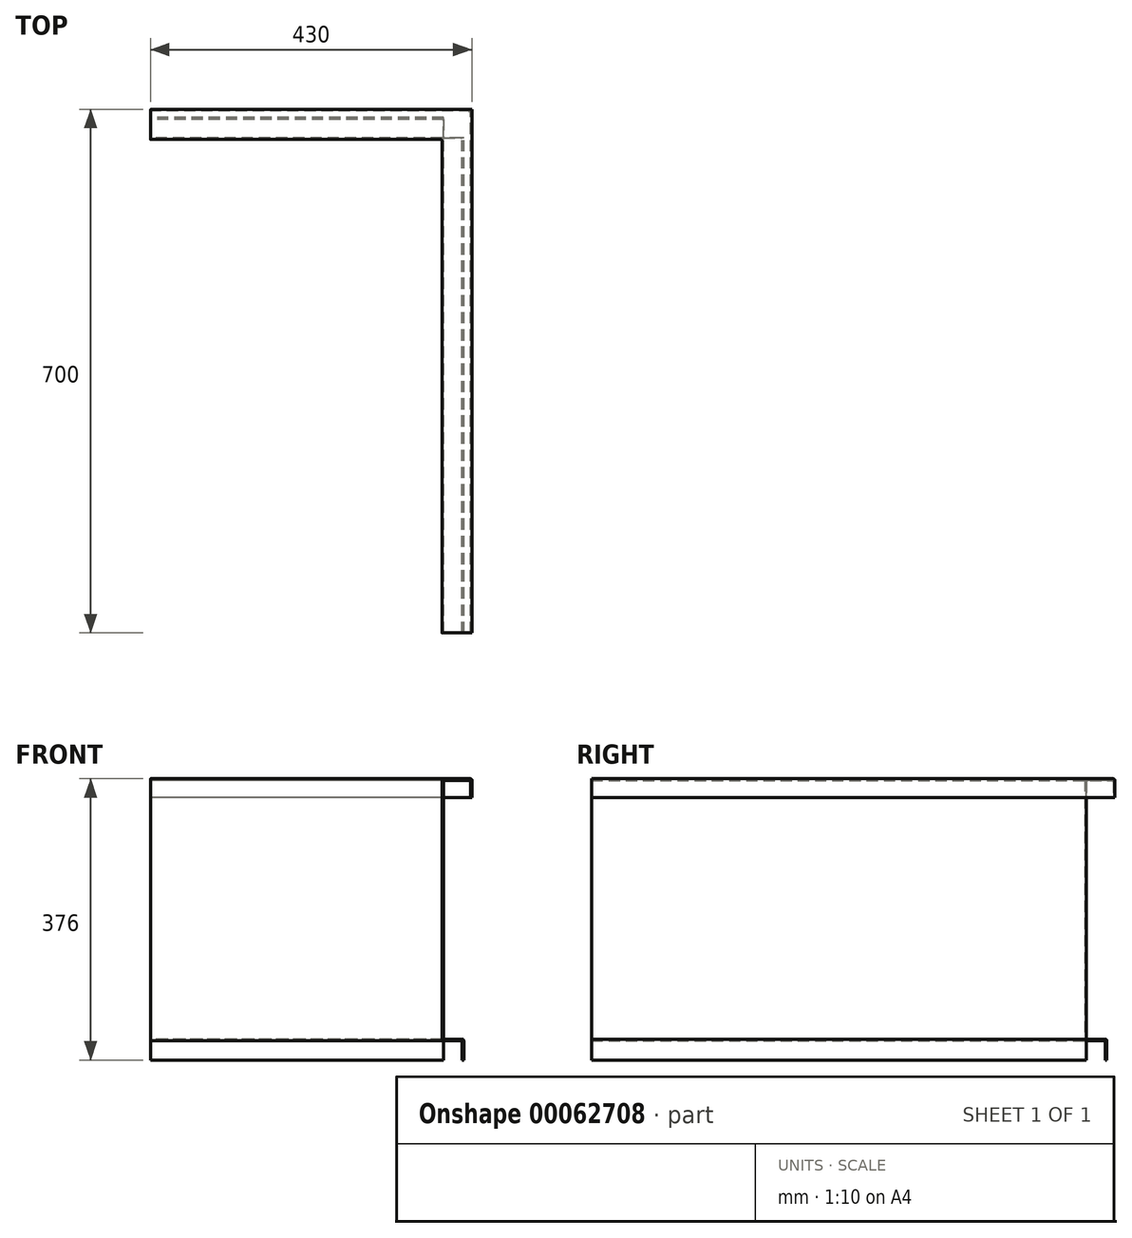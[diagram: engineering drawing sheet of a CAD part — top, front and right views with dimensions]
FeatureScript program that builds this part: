
annotation { "Feature Type Name" : "Feature", "Feature Type Description" : "" }
export const myFeature = defineFeature(function(context is Context, id is Id, definition is map)
    precondition{}
    {
        {
            var Q0;
            Q0=qCreatedBy(makeId("Front.planeOp"),FACE);
            var sketch = newSketch(context, id + "F0", { "sketchPlane" : qUnion([Q0])});
            skLineSegment(sketch, "E0", {"start": v(38, -25) * mm, "end": v(38, -2) * mm});
            skLineSegment(sketch, "E1", {"start": v(38, -2) * mm, "end": v(2, -2) * mm});
            skLineSegment(sketch, "E2", {"start": v(2, -2) * mm, "end": v(2, -348) * mm});
            skLineSegment(sketch, "E3", {"start": v(2, -348) * mm, "end": v(29, -348) * mm});
            skLineSegment(sketch, "E4", {"start": v(29, -348) * mm, "end": v(29, -376) * mm});
            skLineSegment(sketch, "E5.0", {"start": v(27, -350) * mm, "end": v(27, -376) * mm});
            skLineSegment(sketch, "E5.1", {"start": v(40, -25) * mm, "end": v(40, 0) * mm});
            skLineSegment(sketch, "E5.2", {"start": v(40, 0) * mm, "end": v(0, 0) * mm});
            skLineSegment(sketch, "E5.3", {"start": v(0, 0) * mm, "end": v(0, -350) * mm});
            skLineSegment(sketch, "E5.4", {"start": v(0, -350) * mm, "end": v(27, -350) * mm});
            skLineSegment(sketch, "E6", {"start": v(27, -376) * mm, "end": v(29, -376) * mm});
            skLineSegment(sketch, "E7", {"start": v(38, -25) * mm, "end": v(40, -25) * mm});
            skSolve(sketch);
        }
        {
            var Q0;
            Q0=qCreatedBy(makeId("Top.planeOp"),FACE);
            var sketch = newSketch(context, id + "F1", { "sketchPlane" : qUnion([Q0])});
            skLineSegment(sketch, "E8", {"start": v(0, 0) * mm, "end": v(0, 660) * mm});
            skLineSegment(sketch, "E9", {"start": v(0, 660) * mm, "end": v(-390, 660) * mm});
            skSolve(sketch);
        }
        {
            var Q0;
            Q0=qSketchRegion(id+"F0",true);
            var Q1;
            Q1=qConstructionFilter(qBodyType(qCreatedBy(id+"F1",EDGE),BodyType.WIRE),ConstructionObject.NO);
            sweep(context, id + "F2", {"profiles" : qUnion([Q0]), "path" : qUnion([Q1])});
        }
        {
            var Q0;
            Q0=makeQuery(id+"F2.opSweep","SWEPT_FACE",FACE,{"disambiguationData":[OSD([sQuery(id+"F0.wireOp",EDGE,"E3"),sQuery(id+"F1.wireOp",EDGE,"E8")])]});
            var sketch = newSketch(context, id + "F3", { "sketchPlane" : qUnion([Q0])});
            skLineSegment(sketch, "E10", {"start": v(2, 662) * mm, "end": v(29, 662) * mm});
            skLineSegment(sketch, "E11", {"start": v(29, 662) * mm, "end": v(29, 689) * mm});
            skLineSegment(sketch, "E12", {"start": v(29, 689) * mm, "end": v(2, 689) * mm});
            skLineSegment(sketch, "E13", {"start": v(2, 689) * mm, "end": v(2, 662) * mm});
            skSolve(sketch);
        }
        {
            var Q0;
            Q0=qSketchRegion(id+"F3",true);
            extrude(context, id + "F4", {"entities" : qUnion([Q0]), "operationType" : NewBodyOperationType.REMOVE, "oppositeDirection" : true, "depth" : 30 * mm});
        }
        {
            var Q0;
            Q0=makeQuery(id+"F2.opSweep","SWEPT_EDGE",EDGE,{"disambiguationData":[OSD([sQuery(id+"F0.wireOp",EDGE,"E3"),sQuery(id+"F0.wireOp",EDGE,"E4"),sQuery(id+"F1.wireOp",EDGE,"E8")])]});
            var Q1;
            Q1=makeQuery(id+"F2.opSweep","SWEPT_EDGE",EDGE,{"disambiguationData":[OSD([sQuery(id+"F0.wireOp",EDGE,"E3"),sQuery(id+"F0.wireOp",EDGE,"E4"),sQuery(id+"F1.wireOp",EDGE,"E9")])]});
            var Q2;
            Q2=makeQuery(id+"F2.opSweep","SWEPT_EDGE",EDGE,{"disambiguationData":[OSD([sQuery(id+"F0.wireOp",EDGE,"E5.1"),sQuery(id+"F0.wireOp",EDGE,"E5.2"),sQuery(id+"F1.wireOp",EDGE,"E9")])]});
            var Q3;
            Q3=makeQuery(id+"F2.opSweep","SWEPT_EDGE",EDGE,{"disambiguationData":[OSD([sQuery(id+"F0.wireOp",EDGE,"E5.1"),sQuery(id+"F0.wireOp",EDGE,"E5.2"),sQuery(id+"F1.wireOp",EDGE,"E8")])]});
            var Q4;
            Q4=makeQuery(id+"F2.opSweep","MID_CAP_EDGE",EDGE,{"disambiguationData":[OSD([sQuery(id+"F0.wireOp",EDGE,"E2"),sQuery(id+"F1.wireOp",VERTEX,"E9.start")])],"capPos":1.0});
            var Q5;
            Q5=makeQuery(id+"F2.opSweep","SWEPT_EDGE",EDGE,{"disambiguationData":[OSD([sQuery(id+"F0.wireOp",EDGE,"E5.3"),sQuery(id+"F0.wireOp",EDGE,"E5.4"),sQuery(id+"F1.wireOp",EDGE,"E8")])]});
            var Q6;
            Q6=makeQuery(id+"F2.opSweep","SWEPT_EDGE",EDGE,{"disambiguationData":[OSD([sQuery(id+"F0.wireOp",EDGE,"E5.3"),sQuery(id+"F0.wireOp",EDGE,"E5.4"),sQuery(id+"F1.wireOp",EDGE,"E9")])]});
            var Q7;
            Q7=makeQuery(id+"F2.opSweep","SWEPT_EDGE",EDGE,{"disambiguationData":[OSD([sQuery(id+"F0.wireOp",EDGE,"E5.2"),sQuery(id+"F0.wireOp",EDGE,"E5.3"),sQuery(id+"F1.wireOp",EDGE,"E9")])]});
            var Q8;
            Q8=makeQuery(id+"F2.opSweep","SWEPT_EDGE",EDGE,{"disambiguationData":[OSD([sQuery(id+"F0.wireOp",EDGE,"E5.2"),sQuery(id+"F0.wireOp",EDGE,"E5.3"),sQuery(id+"F1.wireOp",EDGE,"E8")])]});
            var Q9;
            Q9=makeQuery(id+"F2.opSweep","SWEPT_EDGE",EDGE,{"disambiguationData":[OSD([sQuery(id+"F0.wireOp",EDGE,"E1"),sQuery(id+"F0.wireOp",EDGE,"E2"),sQuery(id+"F1.wireOp",EDGE,"E8")])]});
            var Q10;
            Q10=makeQuery(id+"F2.opSweep","SWEPT_EDGE",EDGE,{"disambiguationData":[OSD([sQuery(id+"F0.wireOp",EDGE,"E1"),sQuery(id+"F0.wireOp",EDGE,"E2"),sQuery(id+"F1.wireOp",EDGE,"E9")])]});
            var Q11;
            Q11=makeQuery(id+"F2.opSweep","SWEPT_EDGE",EDGE,{"disambiguationData":[OSD([sQuery(id+"F0.wireOp",EDGE,"E0"),sQuery(id+"F0.wireOp",EDGE,"E1"),sQuery(id+"F1.wireOp",EDGE,"E8")])]});
            var Q12;
            Q12=makeQuery(id+"F2.opSweep","SWEPT_EDGE",EDGE,{"disambiguationData":[OSD([sQuery(id+"F0.wireOp",EDGE,"E0"),sQuery(id+"F0.wireOp",EDGE,"E1"),sQuery(id+"F1.wireOp",EDGE,"E9")])]});
            var Q13;
            Q13=makeQuery(id+"F2.opSweep","SWEPT_EDGE",EDGE,{"disambiguationData":[OSD([sQuery(id+"F0.wireOp",EDGE,"E5.0"),sQuery(id+"F0.wireOp",EDGE,"E5.4"),sQuery(id+"F1.wireOp",EDGE,"E9")])]});
            var Q14;
            Q14=makeQuery(id+"F2.opSweep","SWEPT_EDGE",EDGE,{"disambiguationData":[OSD([sQuery(id+"F0.wireOp",EDGE,"E5.0"),sQuery(id+"F0.wireOp",EDGE,"E5.4"),sQuery(id+"F1.wireOp",EDGE,"E8")])]});
            var Q15;
            Q15=makeQuery(id+"F2.opSweep","MID_CAP_EDGE",EDGE,{"disambiguationData":[OSD([sQuery(id+"F0.wireOp",EDGE,"E5.3"),sQuery(id+"F1.wireOp",VERTEX,"E9.start")])],"capPos":1.0});
            fillet(context, id + "F5", {"entities" : qUnion([Q0, Q1, Q2, Q3, Q4, Q5, Q6, Q7, Q8, Q9, Q10, Q11, Q12, Q13, Q14, Q15]), "radius" : 2 * mm, "tangentPropagation" : true, "allowEdgeOverflow" : false});
        }
    });
